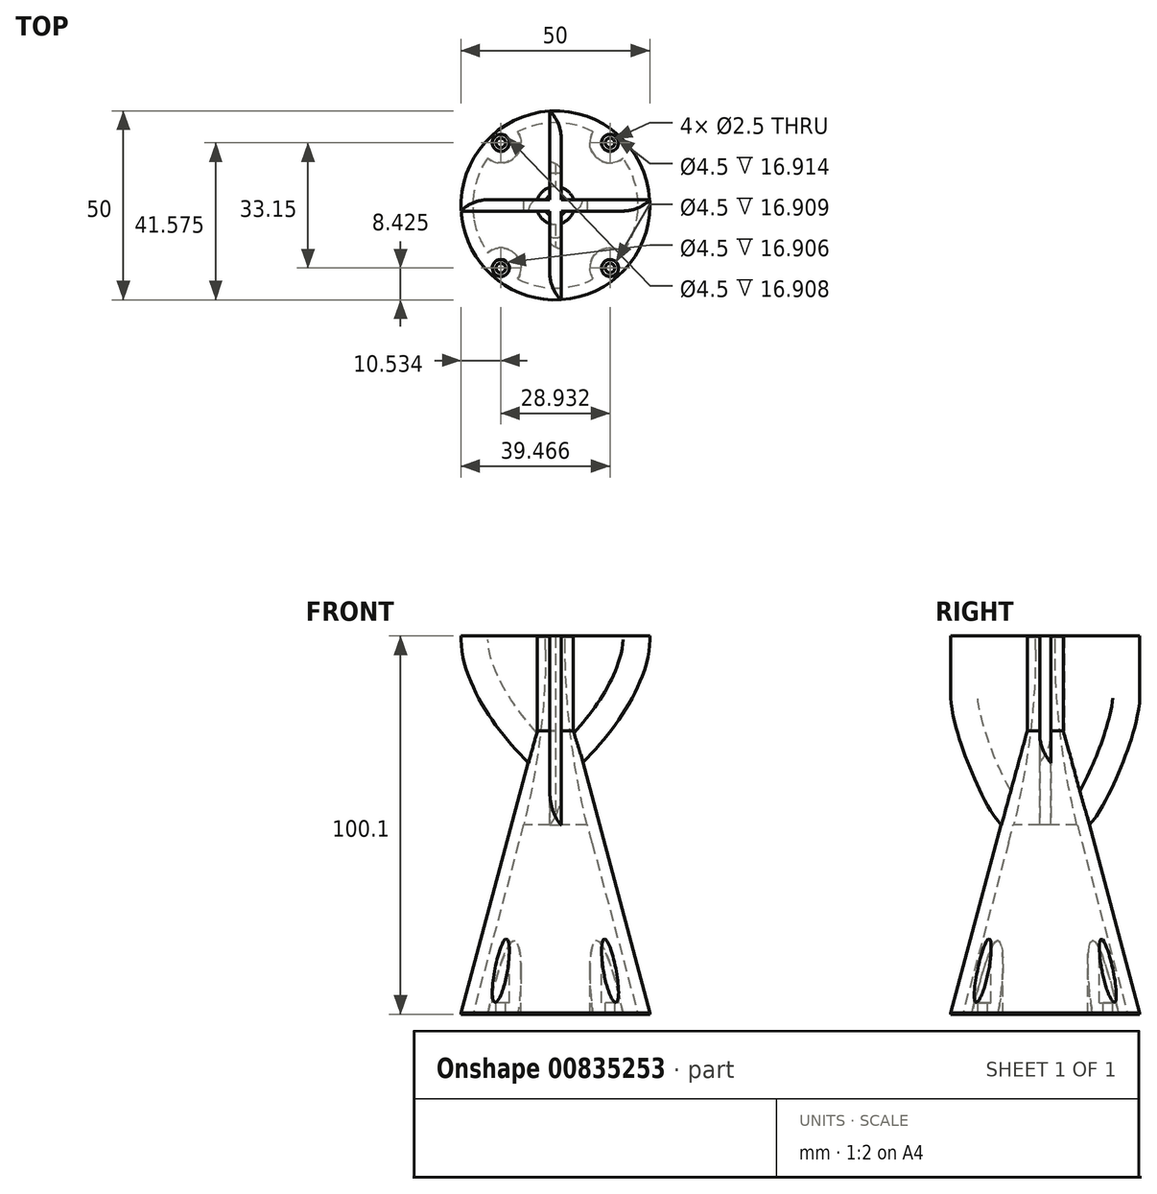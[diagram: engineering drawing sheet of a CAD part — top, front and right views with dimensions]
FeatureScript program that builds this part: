
annotation { "Feature Type Name" : "Feature", "Feature Type Description" : "" }
export const myFeature = defineFeature(function(context is Context, id is Id, definition is map)
    precondition{}
    {
        {
            var Q0;
            Q0=qCreatedBy(makeId("Top.planeOp"),FACE);
            var sketch = newSketch(context, id + "F0", { "sketchPlane" : qUnion([Q0])});
            skCircle(sketch, "E0", {"center": v(0, 0) * mm, "radius": 25 * mm});
            skSolve(sketch);
        }
        {
            var Q0;
            Q0=makeQuery(id+"F0.imprint","IMPRINT",FACE,{"disambiguationData":[TD([[makeQuery(id+"F0.imprint","IMPRINT",EDGE,{"derivedFrom":sQuery(id+"F0.wireOp",EDGE,"E0")}),1.0]])]});
            extrude(context, id + "F1", {"entities" : qUnion([Q0]), "depth" : 20 * mm, "offsetDistance" : 25 * mm});
        }
        {
            var Q0;
            Q0=makeQuery(id+"F1.opExtrude","CAP_FACE",FACE,{"disambiguationData":[OSD([sQuery(id+"F0.wireOp",EDGE,"E0")])],"isStart":false});
            var sketch = newSketch(context, id + "F2", { "sketchPlane" : qUnion([Q0])});
            skCircle(sketch, "E1", {"center": v(-14.47, -16.57) * mm, "radius": 3 * mm});
            skPoint(sketch, "E1.first.point", {"position": v(-16.44, -18.84) * mm});
            skPoint(sketch, "E1.second.point", {"position": v(-12.8, -14.08) * mm});
            skPoint(sketch, "E1.third.point", {"position": v(-15.23, -13.67) * mm});
            skCircle(sketch, "E2", {"center": v(-14.47, -16.57) * mm, "radius": 1.25 * mm});
            skCircle(sketch, "E3.MirrorC", {"center": v(-14.47, 16.57) * mm, "radius": 1.25 * mm});
            skCircle(sketch, "E4.MirrorC", {"center": v(-14.47, 16.57) * mm, "radius": 3 * mm});
            skCircle(sketch, "E5.MirrorC", {"center": v(14.47, -16.57) * mm, "radius": 1.25 * mm});
            skCircle(sketch, "E6.MirrorC", {"center": v(14.47, -16.57) * mm, "radius": 3 * mm});
            skCircle(sketch, "E7.MirrorC", {"center": v(14.47, 16.57) * mm, "radius": 3 * mm});
            skCircle(sketch, "E8.MirrorC", {"center": v(14.47, 16.57) * mm, "radius": 1.25 * mm});
            skSolve(sketch);
        }
        {
            var Q0;
            {var subQ3=sQuery(id+"F2.wireOp",EDGE,"E1");Q0=makeQuery(id+"F2.imprint","IMPRINT",FACE,{"disambiguationData":[TD([[makeQuery(id+"F2.imprint","IMPRINT",EDGE,{"derivedFrom":subQ3}),-1.0]])]});}
            var Q1;
            Q1=makeQuery(id+"F2.imprint","IMPRINT",FACE,{"disambiguationData":[TD([[makeQuery(id+"F2.imprint","IMPRINT",EDGE,{"derivedFrom":sQuery(id+"F2.wireOp",EDGE,"E1")}),1.0]])]});
            var Q2;
            Q2=makeQuery(id+"F2.imprint","IMPRINT",FACE,{"disambiguationData":[TD([[makeQuery(id+"F2.imprint","IMPRINT",EDGE,{"derivedFrom":sQuery(id+"F2.wireOp",EDGE,"E2")}),1.0]])]});
            var Q3;
            Q3=makeQuery(id+"F2.imprint","IMPRINT",FACE,{"disambiguationData":[TD([[makeQuery(id+"F2.imprint","IMPRINT",EDGE,{"derivedFrom":sQuery(id+"F2.wireOp",EDGE,"E5.MirrorC")}),-1.0]])]});
            var Q4;
            Q4=makeQuery(id+"F2.imprint","IMPRINT",FACE,{"disambiguationData":[TD([[makeQuery(id+"F2.imprint","IMPRINT",EDGE,{"derivedFrom":sQuery(id+"F2.wireOp",EDGE,"E5.MirrorC")}),1.0]])]});
            var Q5;
            Q5=makeQuery(id+"F2.imprint","IMPRINT",FACE,{"disambiguationData":[TD([[makeQuery(id+"F2.imprint","IMPRINT",EDGE,{"derivedFrom":sQuery(id+"F2.wireOp",EDGE,"E7.MirrorC")}),1.0]])]});
            var Q6;
            Q6=makeQuery(id+"F2.imprint","IMPRINT",FACE,{"disambiguationData":[TD([[makeQuery(id+"F2.imprint","IMPRINT",EDGE,{"derivedFrom":sQuery(id+"F2.wireOp",EDGE,"E8.MirrorC")}),1.0]])]});
            var Q7;
            Q7=makeQuery(id+"F2.imprint","IMPRINT",FACE,{"disambiguationData":[TD([[makeQuery(id+"F2.imprint","IMPRINT",EDGE,{"derivedFrom":sQuery(id+"F2.wireOp",EDGE,"E3.MirrorC")}),1.0]])]});
            var Q8;
            Q8=makeQuery(id+"F2.imprint","IMPRINT",FACE,{"disambiguationData":[TD([[makeQuery(id+"F2.imprint","IMPRINT",EDGE,{"derivedFrom":sQuery(id+"F2.wireOp",EDGE,"E3.MirrorC")}),-1.0]])]});
            extrude(context, id + "F3", {"entities" : qUnion([Q0, Q1, Q2, Q3, Q4, Q5, Q6, Q7, Q8]), "operationType" : NewBodyOperationType.ADD, "depth" : 55 * mm, "offsetDistance" : 25 * mm});
        }
        {
            var Q0;
            Q0=makeQuery(id+"F3.opExtrude","CAP_FACE",FACE,{"disambiguationData":[OSD([sQuery(id+"F0.wireOp",EDGE,"E0")])],"isStart":false});
            chamfer(context, id + "F4", {"entities" : qUnion([Q0]), "chamferType" : ChamferType.OFFSET_ANGLE, "width" : 20 * mm, "oppositeDirection" : false, "angle" : 75 * degree, "tangentPropagation" : true});
        }
        {
            var Q0;
            Q0=sQuery(id+"F2.wireOp",VERTEX,"E7.MirrorC.center");
            var Q1;
            Q1=sQuery(id+"F2.wireOp",VERTEX,"E5.MirrorC.center");
            var Q2;
            Q2=sQuery(id+"F2.wireOp",VERTEX,"E1.center");
            var Q3;
            Q3=sQuery(id+"F2.wireOp",VERTEX,"E3.MirrorC.center");
            var Q4;
            Q4=makeQuery(id+"F1.opExtrude","SWEPT_BODY",BODY,{"disambiguationData":[OSD([sQuery(id+"F0.wireOp",EDGE,"E0")])]});
            hole(context, id + "F5", {"style" : HoleStyle.C_BORE, "endStyle" : HoleEndStyle.THROUGH, "holeDiameter" : 2.5 * mm, "cBoreDiameter" : 4.5 * mm, "cBoreDepth" : .1 * mm, "majorDiameter" : 5 * mm, "isTappedThrough" : true, "tappedDepth" : 12 * mm, "tapClearance" : 3, "locations" : qUnion([Q0, Q1, Q2, Q3]), "scope" : qUnion([Q4])});
        }
        {
            var Q0;
            Q0=makeQuery(id+"F3.opExtrude","CAP_FACE",FACE,{"disambiguationData":[OSD([sQuery(id+"F0.wireOp",EDGE,"E0")])],"isStart":false});
            extrude(context, id + "F6", {"entities" : qUnion([Q0]), "operationType" : NewBodyOperationType.ADD, "depth" : 25 * mm, "offsetDistance" : 25 * mm});
        }
        {
            var Q0;
            Q0=makeQuery(id+"F6.opExtrude","CAP_FACE",FACE,{"disambiguationData":[OSD([sQuery(id+"F0.wireOp",EDGE,"E0")])],"isStart":false});
            var sketch = newSketch(context, id + "F7", { "sketchPlane" : qUnion([Q0])});
            skCircle(sketch, "E9", {"center": v(0, 0) * mm, "radius": 3 * mm});
            skSolve(sketch);
        }
        {
            var Q0;
            Q0=qCreatedBy(makeId("Front.planeOp"),FACE);
            var sketch = newSketch(context, id + "F8", { "sketchPlane" : qUnion([Q0])});
            skLineSegment(sketch, "E10", {"start": v(0, 100.1) * mm, "end": v(0, 0) * mm, "construction": true});
            skSolve(sketch);
        }
        {
            var Q0;
            Q0=makeQuery(id+"F1.opExtrude","CAP_FACE",FACE,{"disambiguationData":[OSD([sQuery(id+"F0.wireOp",EDGE,"E0")])],"isStart":true});
            var Q1;
            Q1=makeQuery(id+"F1.opExtrude","SWEPT_BODY",BODY,{"disambiguationData":[OSD([sQuery(id+"F0.wireOp",EDGE,"E0")])]});
            shell(context, id + "F9", {"entities" : qUnion([Q0]), "parts" : qUnion([Q1]), "thickness" : 3.1 * mm});
        }
        {
            var Q0;
            Q0=makeQuery(id+"F7.imprint","IMPRINT",FACE,{"disambiguationData":[TD([[makeQuery(id+"F7.imprint","IMPRINT",EDGE,{"derivedFrom":sQuery(id+"F7.wireOp",EDGE,"E9")}),1.0]])]});
            var Q1;
            Q1=sQuery(id+"F7.wireOp",EDGE,"E9");
            extrude(context, id + "F10", {"entities" : qUnion([Q0]), "operationType" : NewBodyOperationType.REMOVE, "surfaceEntities" : qUnion([Q1]), "oppositeDirection" : true, "depth" : 30 * mm, "offsetDistance" : 25 * mm});
        }
        {
            var Q0;
            {var subQ0=sQuery(id+"F0.wireOp",EDGE,"E0");Q0=makeQuery(id+"F10.boolean.opBoolean","INTERSECT",EDGE,{"derivedFrom":[makeQuery(id+"F9.opShell","OFFSET_FACE",FACE,{"disambiguationData":[OSD([subQ0]),TDD([makeQuery(id+"F4.opChamfer","BLEND_FACE",FACE,{"disambiguationData":[OSD([subQ0])]})])]}),makeQuery(id+"F10.opExtrude","SWEPT_FACE",FACE,{"disambiguationData":[OSD([sQuery(id+"F7.wireOp",EDGE,"E9")])]})]});}
            fillet(context, id + "F11", {"entities" : qUnion([Q0]), "radius" : 197 * mm, "tangentPropagation" : true, "allowEdgeOverflow" : false});
        }
        {
            var Q0;
            Q0=qCreatedBy(makeId("Right.planeOp"),FACE);
            var sketch = newSketch(context, id + "F12", { "sketchPlane" : qUnion([Q0])});
            skLineSegment(sketch, "E11.bottom", {"start": v(0, 100.1) * mm, "end": v(-25, 100.1) * mm});
            skLineSegment(sketch, "E11.top", {"start": v(0, 50.1) * mm, "end": v(-25, 50.1) * mm});
            skLineSegment(sketch, "E11.left", {"start": v(0, 100.1) * mm, "end": v(0, 50.1) * mm});
            skLineSegment(sketch, "E11.right", {"start": v(-25, 100.1) * mm, "end": v(-25, 50.1) * mm});
            skLineSegment(sketch, "E12.MirrorCS", {"start": v(25, 100.1) * mm, "end": v(25, 50.1) * mm});
            skLineSegment(sketch, "E13.MirrorCS", {"start": v(0, 50.1) * mm, "end": v(25, 50.1) * mm});
            skLineSegment(sketch, "E14.MirrorCS", {"start": v(0, 100.1) * mm, "end": v(25, 100.1) * mm});
            skSolve(sketch);
        }
        {
            var Q0;
            Q0=qCreatedBy(makeId("Front.planeOp"),FACE);
            var sketch = newSketch(context, id + "F13", { "sketchPlane" : qUnion([Q0])});
            skLineSegment(sketch, "E15.bottom", {"start": v(0, 100.1) * mm, "end": v(-25, 100.1) * mm});
            skLineSegment(sketch, "E15.top", {"start": v(0, 50.1) * mm, "end": v(-25, 50.1) * mm});
            skLineSegment(sketch, "E15.left", {"start": v(0, 100.1) * mm, "end": v(0, 50.1) * mm});
            skLineSegment(sketch, "E15.right", {"start": v(-25, 100.1) * mm, "end": v(-25, 50.1) * mm});
            skLineSegment(sketch, "E16.MirrorCS", {"start": v(0, 100.1) * mm, "end": v(25, 100.1) * mm});
            skLineSegment(sketch, "E17.MirrorCS", {"start": v(25, 100.1) * mm, "end": v(25, 50.1) * mm});
            skLineSegment(sketch, "E18.MirrorCS", {"start": v(0, 50.1) * mm, "end": v(25, 50.1) * mm});
            skSolve(sketch);
        }
        {
            var Q0;
            Q0=makeQuery(id+"F13.imprint","IMPRINT",FACE,{"disambiguationData":[TD([[makeQuery(id+"F13.imprint","IMPRINT",EDGE,{"derivedFrom":sQuery(id+"F13.wireOp",EDGE,"E15.left")}),1.0]])]});
            var Q1;
            Q1=makeQuery(id+"F13.imprint","IMPRINT",FACE,{"disambiguationData":[TD([[makeQuery(id+"F13.imprint","IMPRINT",EDGE,{"derivedFrom":sQuery(id+"F13.wireOp",EDGE,"E15.bottom")}),1.0]])]});
            extrude(context, id + "F14", {"entities" : qUnion([Q0, Q1]), "operationType" : NewBodyOperationType.ADD, "depth" : 1.5 * mm, "offsetDistance" : 25 * mm});
        }
        {
            var Q0;
            Q0 = qSketchRegion(id + "F13", true);
            extrude(context, id + "F15", {"entities" : qUnion([Q0]), "operationType" : NewBodyOperationType.ADD, "oppositeDirection" : true, "depth" : 1.5 * mm, "offsetDistance" : 25 * mm});
        }
        {
            var Q0;
            Q0=makeQuery(id+"F12.imprint","IMPRINT",FACE,{"disambiguationData":[TD([[makeQuery(id+"F12.imprint","IMPRINT",EDGE,{"derivedFrom":sQuery(id+"F12.wireOp",EDGE,"E11.bottom")}),1.0]])]});
            var Q1;
            Q1=makeQuery(id+"F12.imprint","IMPRINT",FACE,{"disambiguationData":[TD([[makeQuery(id+"F12.imprint","IMPRINT",EDGE,{"derivedFrom":sQuery(id+"F12.wireOp",EDGE,"E11.left")}),1.0]])]});
            extrude(context, id + "F16", {"entities" : qUnion([Q0, Q1]), "operationType" : NewBodyOperationType.ADD, "depth" : 1.5 * mm, "offsetDistance" : 25 * mm});
        }
        {
            var Q0;
            {var subQ6=sQuery(id+"F12.wireOp",EDGE,"E13.MirrorCS");var subQ7=sQuery(id+"F12.wireOp",EDGE,"E11.top");var subQ8=sQuery(id+"F12.wireOp",EDGE,"E14.MirrorCS");var subQ9=sQuery(id+"F12.wireOp",EDGE,"E11.bottom");var subQ10=sQuery(id+"F12.wireOp",EDGE,"E11.right");Q0=makeQuery(id+"F16.boolean.opBoolean","SPLIT",FACE,{"disambiguationData":[TD([makeQuery(id+"F16.opExtrude","SWEPT_FACE",FACE,{"disambiguationData":[OSD([subQ10])]})])],"derivedFrom":makeQuery(id+"F16.opExtrude","CAP_FACE",FACE,{"disambiguationData":[OSD([subQ9,subQ7,subQ10,sQuery(id+"F12.wireOp",EDGE,"E12.MirrorCS"),subQ6,subQ8])],"isStart":true})});}
            var Q1;
            {var subQ6=sQuery(id+"F12.wireOp",EDGE,"E13.MirrorCS");var subQ7=sQuery(id+"F12.wireOp",EDGE,"E11.top");var subQ8=sQuery(id+"F12.wireOp",EDGE,"E14.MirrorCS");var subQ9=sQuery(id+"F12.wireOp",EDGE,"E11.bottom");var subQ10=sQuery(id+"F12.wireOp",EDGE,"E12.MirrorCS");Q1=makeQuery(id+"F16.boolean.opBoolean","SPLIT",FACE,{"disambiguationData":[TD([makeQuery(id+"F16.opExtrude","SWEPT_FACE",FACE,{"disambiguationData":[OSD([subQ10])]})])],"derivedFrom":makeQuery(id+"F16.opExtrude","CAP_FACE",FACE,{"disambiguationData":[OSD([subQ9,subQ7,sQuery(id+"F12.wireOp",EDGE,"E11.right"),subQ10,subQ6,subQ8])],"isStart":true})});}
            extrude(context, id + "F17", {"entities" : qUnion([Q0, Q1]), "operationType" : NewBodyOperationType.ADD, "depth" : 1.5 * mm, "offsetDistance" : 25 * mm});
        }
        {
            var Q0;
            {var subQ0=sQuery(id+"F12.wireOp",EDGE,"E13.MirrorCS");var subQ1=sQuery(id+"F12.wireOp",EDGE,"E12.MirrorCS");Q0=makeQuery(id+"F17.boolean.opBoolean","MERGE",EDGE,{"derivedFrom":[makeQuery(id+"F16.opExtrude","SWEPT_EDGE",EDGE,{"disambiguationData":[OSD([subQ1,subQ0])]}),makeQuery(id+"F17.opExtrude","SWEPT_EDGE",EDGE,{"disambiguationData":[OSD([subQ1,subQ0])]})]});}
            var Q1;
            {var subQ0=sQuery(id+"F13.wireOp",EDGE,"E18.MirrorCS");var subQ1=sQuery(id+"F13.wireOp",EDGE,"E17.MirrorCS");Q1=makeQuery(id+"F15.boolean.opBoolean","MERGE",EDGE,{"derivedFrom":[makeQuery(id+"F14.opExtrude","SWEPT_EDGE",EDGE,{"disambiguationData":[OSD([subQ1,subQ0])]}),makeQuery(id+"F15.opExtrude","SWEPT_EDGE",EDGE,{"disambiguationData":[OSD([subQ1,subQ0])]})]});}
            var Q2;
            {var subQ0=sQuery(id+"F13.wireOp",EDGE,"E15.right");var subQ1=sQuery(id+"F13.wireOp",EDGE,"E15.top");Q2=makeQuery(id+"F15.boolean.opBoolean","MERGE",EDGE,{"derivedFrom":[makeQuery(id+"F14.opExtrude","SWEPT_EDGE",EDGE,{"disambiguationData":[OSD([subQ1,subQ0])]}),makeQuery(id+"F15.opExtrude","SWEPT_EDGE",EDGE,{"disambiguationData":[OSD([subQ1,subQ0])]})]});}
            var Q3;
            {var subQ0=sQuery(id+"F12.wireOp",EDGE,"E11.right");var subQ1=sQuery(id+"F12.wireOp",EDGE,"E11.top");Q3=makeQuery(id+"F17.boolean.opBoolean","MERGE",EDGE,{"derivedFrom":[makeQuery(id+"F16.opExtrude","SWEPT_EDGE",EDGE,{"disambiguationData":[OSD([subQ1,subQ0])]}),makeQuery(id+"F17.opExtrude","SWEPT_EDGE",EDGE,{"disambiguationData":[OSD([subQ1,subQ0])]})]});}
            fillet(context, id + "F18", {"entities" : qUnion([Q0, Q1, Q2, Q3]), "radius" : 49 * mm, "tangentPropagation" : true, "rho" : .3, "crossSection" : FilletCrossSection.CONIC, "allowEdgeOverflow" : false});
        }
        {
            var Q0;
            {var subQ0=sQuery(id+"F13.wireOp",EDGE,"E18.MirrorCS");var subQ1=sQuery(id+"F13.wireOp",EDGE,"E15.top");var subQ3=sQuery(id+"F13.wireOp",EDGE,"E16.MirrorCS");var subQ4=sQuery(id+"F13.wireOp",EDGE,"E15.bottom");var subQ8=sQuery(id+"F13.wireOp",EDGE,"E17.MirrorCS");Q0=makeQuery(id+"F18.opFillet","BLEND_EDGE",EDGE,{"blendedFrom":[makeQuery(id+"F15.boolean.opBoolean","MERGE",EDGE,{"derivedFrom":[makeQuery(id+"F14.opExtrude","SWEPT_EDGE",EDGE,{"disambiguationData":[OSD([subQ8,subQ0])]}),makeQuery(id+"F15.opExtrude","SWEPT_EDGE",EDGE,{"disambiguationData":[OSD([subQ8,subQ0])]})]}),makeQuery(id+"F16.boolean.opBoolean","SPLIT",FACE,{"disambiguationData":[TD([makeQuery(id+"F14.opExtrude","SWEPT_FACE",FACE,{"disambiguationData":[OSD([subQ8])]})])],"derivedFrom":makeQuery(id+"F14.opExtrude","CAP_FACE",FACE,{"disambiguationData":[OSD([subQ4,subQ1,sQuery(id+"F13.wireOp",EDGE,"E15.right"),subQ3,subQ8,subQ0])],"isStart":false})})],"blendedInto":[makeQuery(id+"F16.boolean.opBoolean","SPLIT",FACE,{"disambiguationData":[TD([makeQuery(id+"F14.opExtrude","SWEPT_FACE",FACE,{"disambiguationData":[OSD([subQ8])]})])],"derivedFrom":makeQuery(id+"F14.opExtrude","CAP_FACE",FACE,{"disambiguationData":[OSD([subQ4,subQ1,sQuery(id+"F13.wireOp",EDGE,"E15.right"),subQ3,subQ8,subQ0])],"isStart":false})})]});}
            var Q1;
            {var subQ6=sQuery(id+"F12.wireOp",EDGE,"E13.MirrorCS");var subQ7=sQuery(id+"F12.wireOp",EDGE,"E11.top");var subQ8=sQuery(id+"F12.wireOp",EDGE,"E14.MirrorCS");var subQ9=sQuery(id+"F12.wireOp",EDGE,"E11.bottom");var subQ10=sQuery(id+"F12.wireOp",EDGE,"E11.right");var subQ11=sQuery(id+"F12.wireOp",EDGE,"E12.MirrorCS");Q1=makeQuery(id+"F18.opFillet","BLEND_EDGE",EDGE,{"blendedFrom":[makeQuery(id+"F17.boolean.opBoolean","MERGE",EDGE,{"derivedFrom":[makeQuery(id+"F16.opExtrude","SWEPT_EDGE",EDGE,{"disambiguationData":[OSD([subQ7,subQ10])]}),makeQuery(id+"F17.opExtrude","SWEPT_EDGE",EDGE,{"disambiguationData":[OSD([subQ7,subQ10])]})]}),makeQuery(id+"F17.opExtrude","CAP_FACE",FACE,{"disambiguationData":[OSD([subQ9,subQ7,subQ10,subQ11,subQ6,subQ8]),TDD([makeQuery(id+"F16.boolean.opBoolean","SPLIT",FACE,{"disambiguationData":[TD([makeQuery(id+"F16.opExtrude","SWEPT_FACE",FACE,{"disambiguationData":[OSD([subQ10])]})])],"derivedFrom":makeQuery(id+"F16.opExtrude","CAP_FACE",FACE,{"disambiguationData":[OSD([subQ9,subQ7,subQ10,subQ11,subQ6,subQ8])],"isStart":true})})])],"isStart":false})],"blendedInto":[makeQuery(id+"F17.opExtrude","CAP_FACE",FACE,{"disambiguationData":[OSD([subQ9,subQ7,subQ10,subQ11,subQ6,subQ8]),TDD([makeQuery(id+"F16.boolean.opBoolean","SPLIT",FACE,{"disambiguationData":[TD([makeQuery(id+"F16.opExtrude","SWEPT_FACE",FACE,{"disambiguationData":[OSD([subQ10])]})])],"derivedFrom":makeQuery(id+"F16.opExtrude","CAP_FACE",FACE,{"disambiguationData":[OSD([subQ9,subQ7,subQ10,subQ11,subQ6,subQ8])],"isStart":true})})])],"isStart":false})]});}
            var Q2;
            {var subQ0=sQuery(id+"F13.wireOp",EDGE,"E18.MirrorCS");var subQ1=sQuery(id+"F13.wireOp",EDGE,"E15.top");var subQ3=sQuery(id+"F13.wireOp",EDGE,"E16.MirrorCS");var subQ4=sQuery(id+"F13.wireOp",EDGE,"E15.bottom");var subQ5=sQuery(id+"F13.wireOp",EDGE,"E15.right");Q2=makeQuery(id+"F18.opFillet","BLEND_EDGE",EDGE,{"blendedFrom":[makeQuery(id+"F15.boolean.opBoolean","MERGE",EDGE,{"derivedFrom":[makeQuery(id+"F14.opExtrude","SWEPT_EDGE",EDGE,{"disambiguationData":[OSD([subQ1,subQ5])]}),makeQuery(id+"F15.opExtrude","SWEPT_EDGE",EDGE,{"disambiguationData":[OSD([subQ1,subQ5])]})]}),makeQuery(id+"F16.boolean.opBoolean","SPLIT",FACE,{"disambiguationData":[TD([makeQuery(id+"F14.opExtrude","SWEPT_FACE",FACE,{"disambiguationData":[OSD([subQ5])]})])],"derivedFrom":makeQuery(id+"F15.opExtrude","CAP_FACE",FACE,{"disambiguationData":[OSD([subQ4,subQ1,subQ5,subQ3,sQuery(id+"F13.wireOp",EDGE,"E17.MirrorCS"),subQ0])],"isStart":false})})],"blendedInto":[makeQuery(id+"F16.boolean.opBoolean","SPLIT",FACE,{"disambiguationData":[TD([makeQuery(id+"F14.opExtrude","SWEPT_FACE",FACE,{"disambiguationData":[OSD([subQ5])]})])],"derivedFrom":makeQuery(id+"F15.opExtrude","CAP_FACE",FACE,{"disambiguationData":[OSD([subQ4,subQ1,subQ5,subQ3,sQuery(id+"F13.wireOp",EDGE,"E17.MirrorCS"),subQ0])],"isStart":false})})]});}
            var Q3;
            {var subQ6=sQuery(id+"F12.wireOp",EDGE,"E13.MirrorCS");var subQ7=sQuery(id+"F12.wireOp",EDGE,"E11.top");var subQ8=sQuery(id+"F12.wireOp",EDGE,"E14.MirrorCS");var subQ9=sQuery(id+"F12.wireOp",EDGE,"E11.bottom");var subQ10=sQuery(id+"F12.wireOp",EDGE,"E12.MirrorCS");Q3=makeQuery(id+"F18.opFillet","BLEND_EDGE",EDGE,{"blendedFrom":[makeQuery(id+"F17.boolean.opBoolean","MERGE",EDGE,{"derivedFrom":[makeQuery(id+"F16.opExtrude","SWEPT_EDGE",EDGE,{"disambiguationData":[OSD([subQ10,subQ6])]}),makeQuery(id+"F17.opExtrude","SWEPT_EDGE",EDGE,{"disambiguationData":[OSD([subQ10,subQ6])]})]}),makeQuery(id+"F16.boolean.opBoolean","SPLIT",FACE,{"disambiguationData":[TD([makeQuery(id+"F16.opExtrude","SWEPT_FACE",FACE,{"disambiguationData":[OSD([subQ10])]})])],"derivedFrom":makeQuery(id+"F16.opExtrude","CAP_FACE",FACE,{"disambiguationData":[OSD([subQ9,subQ7,sQuery(id+"F12.wireOp",EDGE,"E11.right"),subQ10,subQ6,subQ8])],"isStart":false})})],"blendedInto":[makeQuery(id+"F16.boolean.opBoolean","SPLIT",FACE,{"disambiguationData":[TD([makeQuery(id+"F16.opExtrude","SWEPT_FACE",FACE,{"disambiguationData":[OSD([subQ10])]})])],"derivedFrom":makeQuery(id+"F16.opExtrude","CAP_FACE",FACE,{"disambiguationData":[OSD([subQ9,subQ7,sQuery(id+"F12.wireOp",EDGE,"E11.right"),subQ10,subQ6,subQ8])],"isStart":false})})]});}
            fillet(context, id + "F19", {"entities" : qUnion([Q0, Q1, Q2, Q3]), "radius" : 10 * mm, "tangentPropagation" : true, "allowEdgeOverflow" : false});
        }
    });
